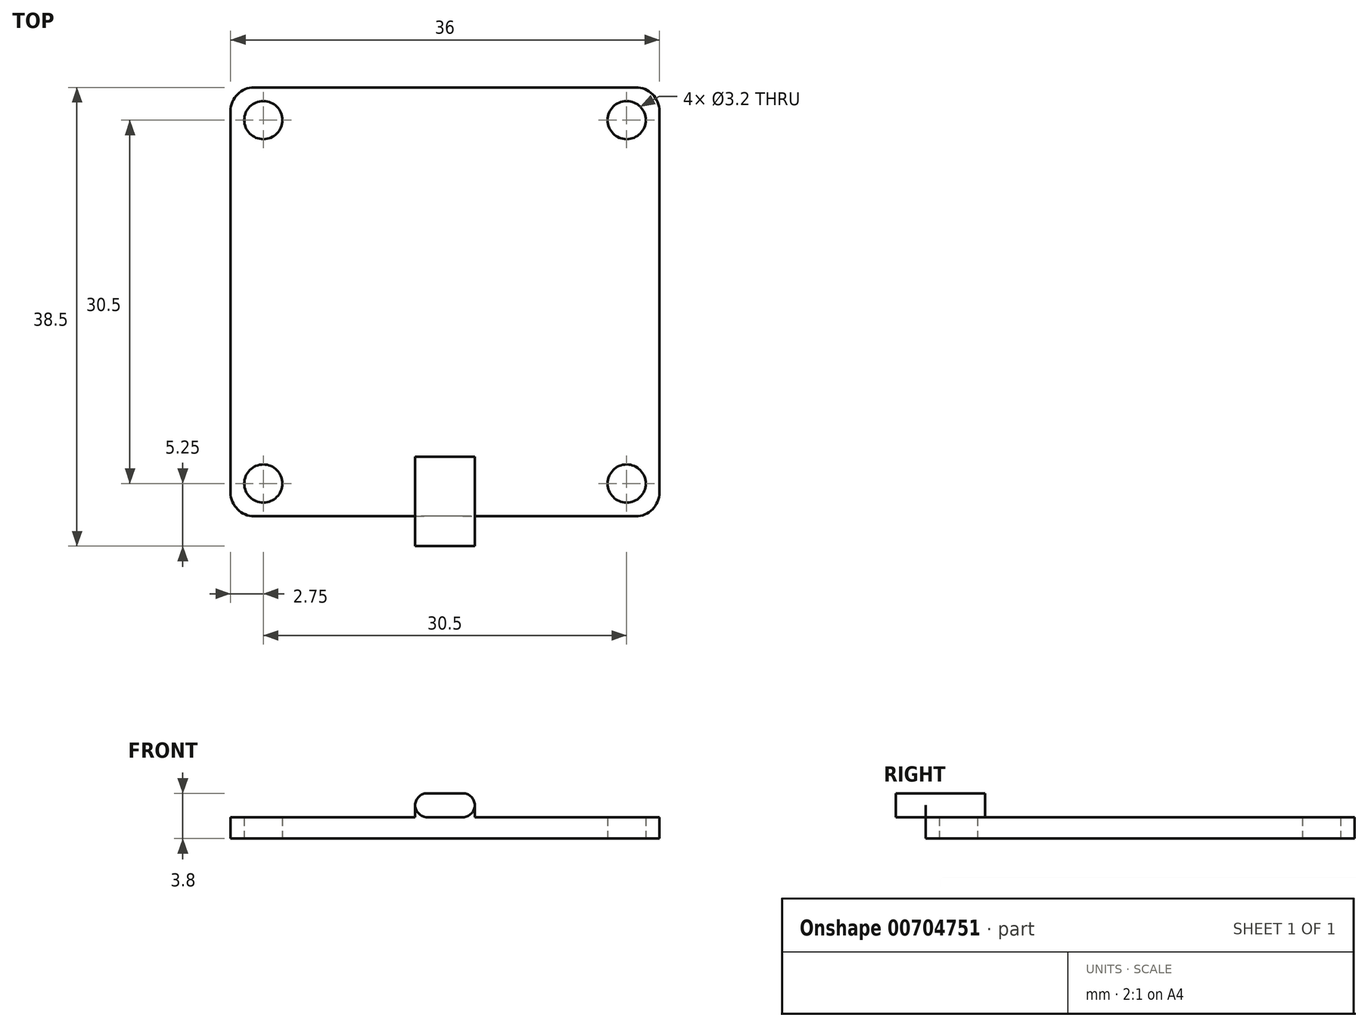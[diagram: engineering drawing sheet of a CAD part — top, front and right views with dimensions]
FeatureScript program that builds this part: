
annotation { "Feature Type Name" : "Feature", "Feature Type Description" : "" }
export const myFeature = defineFeature(function(context is Context, id is Id, definition is map)
    precondition{}
    {
        {
            var Q0;
            Q0=qCreatedBy(makeId("Top.planeOp"),FACE);
            var sketch = newSketch(context, id + "F0", { "sketchPlane" : qUnion([Q0])});
            skLineSegment(sketch, "E0.bottom", {"start": v(18, -18) * mm, "end": v(-18, -18) * mm});
            skLineSegment(sketch, "E0.top", {"start": v(18, 18) * mm, "end": v(-18, 18) * mm});
            skLineSegment(sketch, "E0.left", {"start": v(18, -18) * mm, "end": v(18, 18) * mm});
            skLineSegment(sketch, "E0.right", {"start": v(-18, -18) * mm, "end": v(-18, 18) * mm});
            skPoint(sketch, "E0.middle", {"position": v(0, 0) * mm});
            skCircle(sketch, "E1", {"center": v(-15.25, -15.25) * mm, "radius": 1.6 * mm});
            skCircle(sketch, "E2.MirrorC", {"center": v(-15.25, 15.25) * mm, "radius": 1.6 * mm});
            skCircle(sketch, "E3.MirrorC", {"center": v(15.25, -15.25) * mm, "radius": 1.6 * mm});
            skCircle(sketch, "E4.MirrorC", {"center": v(15.25, 15.25) * mm, "radius": 1.6 * mm});
            skSolve(sketch);
        }
        {
            var Q0;
            Q0=makeQuery(id+"F0.imprint","IMPRINT",FACE,{"disambiguationData":[TD([[makeQuery(id+"F0.imprint","IMPRINT",EDGE,{"derivedFrom":sQuery(id+"F0.wireOp",EDGE,"E0.bottom")}),-1.0]])]});
            extrude(context, id + "F1", {"entities" : qUnion([Q0]), "depth" : 1.8 * mm, "offsetDistance" : 25 * mm});
        }
        {
            var Q0;
            Q0=makeQuery(id+"F1.opExtrude","SWEPT_EDGE",EDGE,{"disambiguationData":[OSD([sQuery(id+"F0.wireOp",EDGE,"E0.bottom"),sQuery(id+"F0.wireOp",EDGE,"E0.right")])]});
            var Q1;
            Q1=makeQuery(id+"F1.opExtrude","SWEPT_EDGE",EDGE,{"disambiguationData":[OSD([sQuery(id+"F0.wireOp",EDGE,"E0.bottom"),sQuery(id+"F0.wireOp",EDGE,"E0.left")])]});
            var Q2;
            Q2=makeQuery(id+"F1.opExtrude","SWEPT_EDGE",EDGE,{"disambiguationData":[OSD([sQuery(id+"F0.wireOp",EDGE,"E0.top"),sQuery(id+"F0.wireOp",EDGE,"E0.left")])]});
            var Q3;
            Q3=makeQuery(id+"F1.opExtrude","SWEPT_EDGE",EDGE,{"disambiguationData":[OSD([sQuery(id+"F0.wireOp",EDGE,"E0.top"),sQuery(id+"F0.wireOp",EDGE,"E0.right")])]});
            fillet(context, id + "F2", {"entities" : qUnion([Q0, Q1, Q2, Q3]), "radius" : 2 * mm, "tangentPropagation" : true, "allowEdgeOverflow" : false});
        }
        {
            var Q0;
            Q0=makeQuery(id+"F1.opExtrude","CAP_FACE",FACE,{"disambiguationData":[OSD([sQuery(id+"F0.wireOp",EDGE,"E0.bottom"),sQuery(id+"F0.wireOp",EDGE,"E0.top"),sQuery(id+"F0.wireOp",EDGE,"E0.left"),sQuery(id+"F0.wireOp",EDGE,"E0.right"),sQuery(id+"F0.wireOp",EDGE,"E1"),sQuery(id+"F0.wireOp",EDGE,"E2.MirrorC"),sQuery(id+"F0.wireOp",EDGE,"E3.MirrorC"),sQuery(id+"F0.wireOp",EDGE,"E4.MirrorC")])],"isStart":false});
            var sketch = newSketch(context, id + "F3", { "sketchPlane" : qUnion([Q0])});
            skLineSegment(sketch, "E5.bottom", {"start": v(2.5, -13) * mm, "end": v(-2.5, -13) * mm});
            skLineSegment(sketch, "E5.top", {"start": v(2.5, -20.5) * mm, "end": v(-2.5, -20.5) * mm});
            skLineSegment(sketch, "E5.left", {"start": v(2.5, -13) * mm, "end": v(2.5, -20.5) * mm});
            skLineSegment(sketch, "E5.right", {"start": v(-2.5, -13) * mm, "end": v(-2.5, -20.5) * mm});
            skPoint(sketch, "E5.middle", {"position": v(0, -16.75) * mm});
            skSolve(sketch);
        }
        {
            var Q0;
            Q0 = qSketchRegion(id + "F3", true);
            extrude(context, id + "F4", {"entities" : qUnion([Q0]), "operationType" : NewBodyOperationType.ADD, "depth" : 2 * mm, "offsetDistance" : 25 * mm});
        }
        {
            var Q0;
            {var subQ0=sQuery(id+"F3.wireOp",EDGE,"E5.right");Q0=makeQuery(id+"F4.boolean.opBoolean","SPLIT",EDGE,{"disambiguationData":[topologyDisambiguationEdgeConnected([makeQuery(id+"F4.opExtrude","CAP_FACE",FACE,{"disambiguationData":[OSD([sQuery(id+"F3.wireOp",EDGE,"E5.bottom"),sQuery(id+"F3.wireOp",EDGE,"E5.top"),sQuery(id+"F3.wireOp",EDGE,"E5.left"),subQ0])],"isStart":true})])],"derivedFrom":makeQuery(id+"F4.opExtrude","CAP_EDGE",EDGE,{"disambiguationData":[OSD([subQ0])],"isStart":true})});}
            var Q1;
            Q1=makeQuery(id+"F4.opExtrude","CAP_EDGE",EDGE,{"disambiguationData":[OSD([sQuery(id+"F3.wireOp",EDGE,"E5.right")])],"isStart":false});
            var Q2;
            Q2=makeQuery(id+"F4.opExtrude","CAP_EDGE",EDGE,{"disambiguationData":[OSD([sQuery(id+"F3.wireOp",EDGE,"E5.left")])],"isStart":false});
            var Q3;
            {var subQ0=sQuery(id+"F3.wireOp",EDGE,"E5.left");Q3=makeQuery(id+"F4.boolean.opBoolean","SPLIT",EDGE,{"disambiguationData":[topologyDisambiguationEdgeConnected([makeQuery(id+"F4.opExtrude","CAP_FACE",FACE,{"disambiguationData":[OSD([sQuery(id+"F3.wireOp",EDGE,"E5.bottom"),sQuery(id+"F3.wireOp",EDGE,"E5.top"),subQ0,sQuery(id+"F3.wireOp",EDGE,"E5.right")])],"isStart":true})])],"derivedFrom":makeQuery(id+"F4.opExtrude","CAP_EDGE",EDGE,{"disambiguationData":[OSD([subQ0])],"isStart":true})});}
            fillet(context, id + "F5", {"entities" : qUnion([Q0, Q1, Q2, Q3]), "radius" : 1 * mm, "tangentPropagation" : true, "allowEdgeOverflow" : false});
        }
    });
